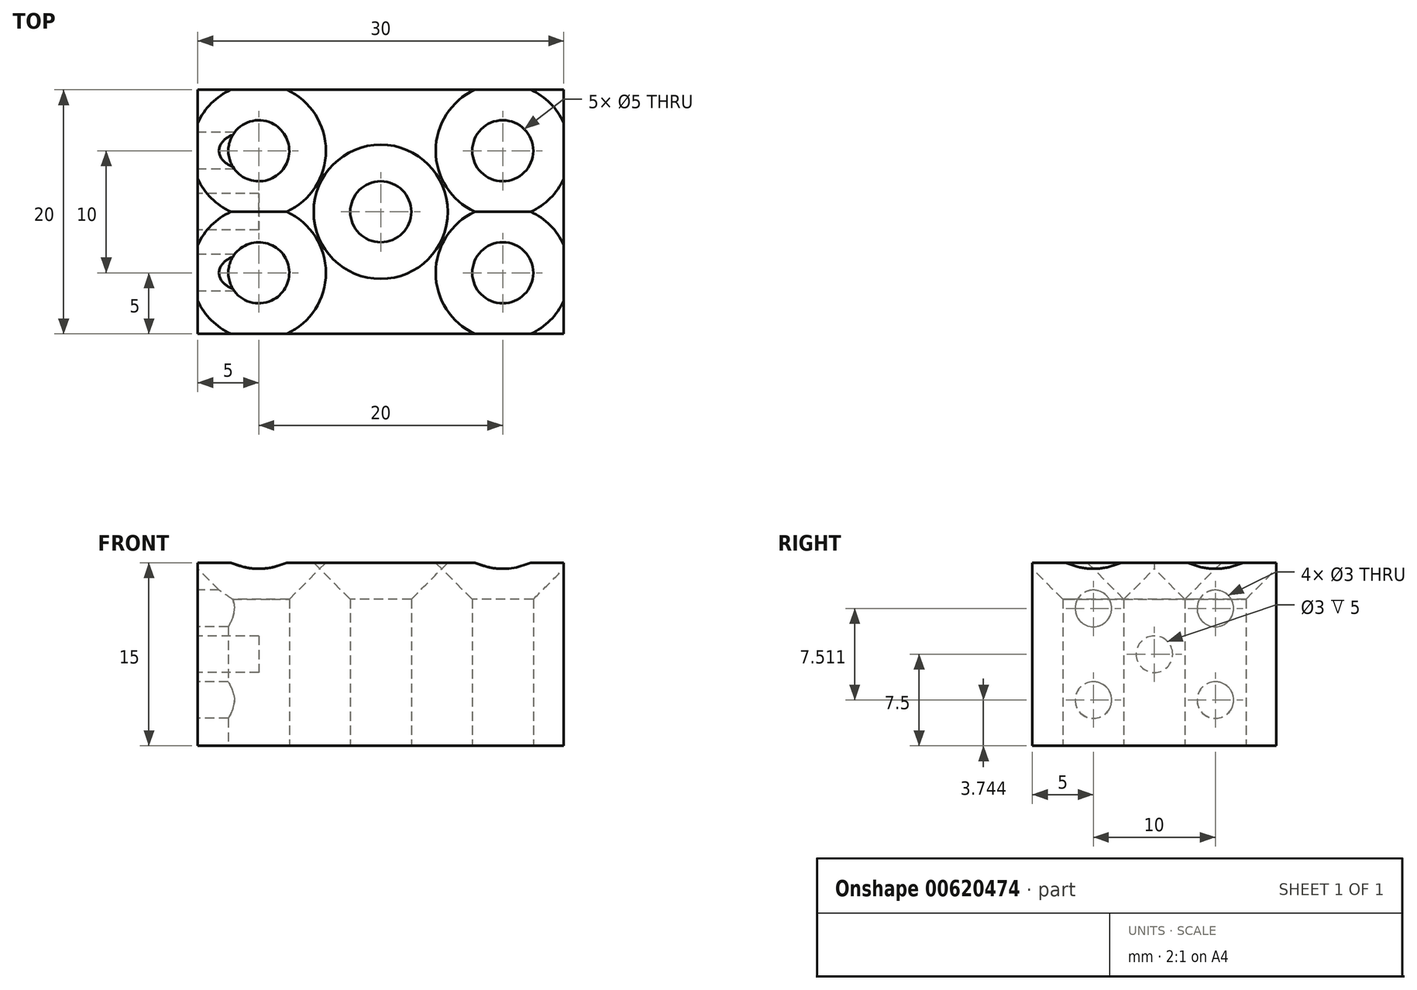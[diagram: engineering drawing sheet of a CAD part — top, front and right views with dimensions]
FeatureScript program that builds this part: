
annotation { "Feature Type Name" : "Feature", "Feature Type Description" : "" }
export const myFeature = defineFeature(function(context is Context, id is Id, definition is map)
    precondition{}
    {
        {
            var Q0;
            Q0=qCreatedBy(makeId("Top.planeOp"),FACE);
            var sketch = newSketch(context, id + "F0", { "sketchPlane" : qUnion([Q0])});
            skCircle(sketch, "E0", {"center": v(0, 0) * mm, "radius": 2.5 * mm});
            skLineSegment(sketch, "E1.bottom", {"start": v(-15, 10) * mm, "end": v(15, 10) * mm});
            skLineSegment(sketch, "E1.top", {"start": v(-15, -10) * mm, "end": v(15, -10) * mm});
            skLineSegment(sketch, "E1.left", {"start": v(-15, 10) * mm, "end": v(-15, -10) * mm});
            skLineSegment(sketch, "E1.right", {"start": v(15, 10) * mm, "end": v(15, -10) * mm});
            skLineSegment(sketch, "E2", {"start": v(-5, 10) * mm, "end": v(-5, -10) * mm, "construction": true});
            skLineSegment(sketch, "E3", {"start": v(-15, 5) * mm, "end": v(-5, 5) * mm, "construction": true});
            skLineSegment(sketch, "E4", {"start": v(-15, 10) * mm, "end": v(-5, 10) * mm});
            skLineSegment(sketch, "E5", {"start": v(-15, 10) * mm, "end": v(-15, 5) * mm});
            skLineSegment(sketch, "E6", {"start": v(-15, 5) * mm, "end": v(-5, 5) * mm});
            skCircle(sketch, "E7", {"center": v(-10, 5) * mm, "radius": 2.5 * mm});
            skCircle(sketch, "E8.MirrorC", {"center": v(-10, -5) * mm, "radius": 2.5 * mm});
            skCircle(sketch, "E9.MirrorC", {"center": v(10, 5) * mm, "radius": 2.5 * mm});
            skCircle(sketch, "E10.MirrorC", {"center": v(10, -5) * mm, "radius": 2.5 * mm});
            skSolve(sketch);
        }
        {
            var Q0;
            Q0=qSketchRegion(id+"F0",true);
            extrude(context, id + "F1", {"entities" : qUnion([Q0]), "depth" : 15 * mm, "offsetDistance" : 25 * mm});
        }
        {
            var Q0;
            Q0=makeQuery(id+"F1.opExtrude","CAP_EDGE",EDGE,{"disambiguationData":[OSD([sQuery(id+"F0.wireOp",EDGE,"E7")])],"isStart":false});
            var Q1;
            Q1=makeQuery(id+"F1.opExtrude","CAP_EDGE",EDGE,{"disambiguationData":[OSD([sQuery(id+"F0.wireOp",EDGE,"E0")])],"isStart":false});
            var Q2;
            Q2=makeQuery(id+"F1.opExtrude","CAP_EDGE",EDGE,{"disambiguationData":[OSD([sQuery(id+"F0.wireOp",EDGE,"E8.MirrorC")])],"isStart":false});
            var Q3;
            Q3=makeQuery(id+"F1.opExtrude","CAP_EDGE",EDGE,{"disambiguationData":[OSD([sQuery(id+"F0.wireOp",EDGE,"E9.MirrorC")])],"isStart":false});
            var Q4;
            Q4=makeQuery(id+"F1.opExtrude","CAP_EDGE",EDGE,{"disambiguationData":[OSD([sQuery(id+"F0.wireOp",EDGE,"E10.MirrorC")])],"isStart":false});
            chamfer(context, id + "F2", {"entities" : qUnion([Q0, Q1, Q2, Q3, Q4]), "width" : 3 * mm, "tangentPropagation" : true});
        }
        {
            var Q0;
            Q0=makeQuery(id+"F1.opExtrude","SWEPT_FACE",FACE,{"disambiguationData":[OSD([sQuery(id+"F0.wireOp",EDGE,"E1.left"),sQuery(id+"F0.wireOp",EDGE,"E5")])]});
            var sketch = newSketch(context, id + "F3", { "sketchPlane" : qUnion([Q0])});
            skLineSegment(sketch, "E11", {"start": v(0, 15) * mm, "end": v(0, 0) * mm, "construction": true});
            skLineSegment(sketch, "E12.0", {"start": v(-10, 15) * mm, "end": v(-10, 0) * mm, "construction": true});
            skLineSegment(sketch, "E13", {"start": v(-10, 7.5) * mm, "end": v(-29.96, 7.5) * mm, "construction": true});
            skCircle(sketch, "E14", {"center": v(0, 7.5) * mm, "radius": 1.5 * mm});
            skLineSegment(sketch, "E15", {"start": v(-10, 15) * mm, "end": v(0, 15) * mm, "construction": true});
            skLineSegment(sketch, "E16", {"start": v(-5, 15) * mm, "end": v(-5, 0) * mm, "construction": true});
            skPoint(sketch, "E16.startSnap0", {"position": v(-5, 15) * mm});
            skLineSegment(sketch, "E17", {"start": v(-10, 7.5) * mm, "end": v(0, 7.5) * mm, "construction": true});
            skLineSegment(sketch, "E18", {"start": v(-5, 15) * mm, "end": v(-5, 7.5) * mm, "construction": true});
            skCircle(sketch, "E19", {"center": v(-5, 11.26) * mm, "radius": 1.5 * mm});
            skCircle(sketch, "E20.MirrorC", {"center": v(-5, 3.74) * mm, "radius": 1.5 * mm});
            skCircle(sketch, "E21.MirrorC", {"center": v(5, 11.26) * mm, "radius": 1.5 * mm});
            skCircle(sketch, "E22.MirrorC", {"center": v(5, 3.74) * mm, "radius": 1.5 * mm});
            skSolve(sketch);
        }
        {
            var Q0;
            Q0 = qSketchRegion(id + "F3", true);
            extrude(context, id + "F4", {"entities" : qUnion([Q0]), "operationType" : NewBodyOperationType.REMOVE, "oppositeDirection" : true, "depth" : 5 * mm, "offsetDistance" : 25 * mm});
        }
    });
